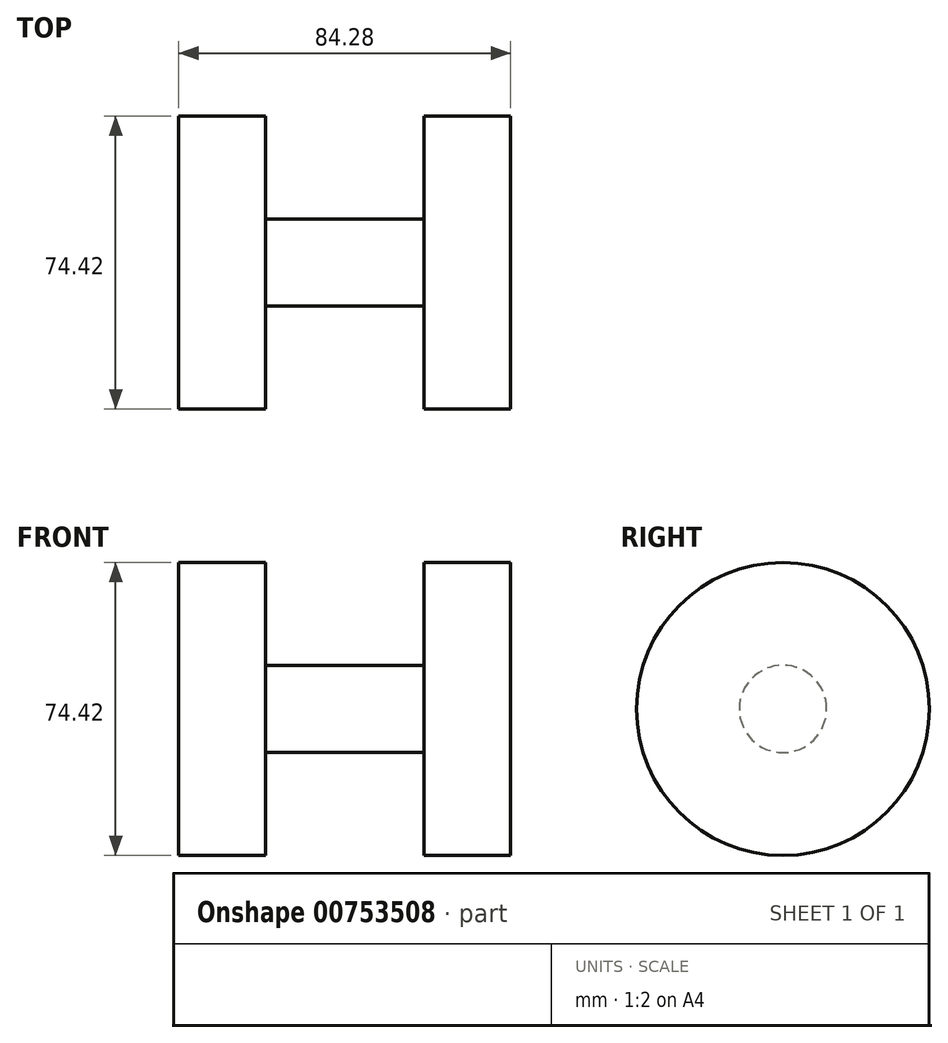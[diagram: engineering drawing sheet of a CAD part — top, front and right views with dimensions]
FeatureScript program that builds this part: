
annotation { "Feature Type Name" : "Feature", "Feature Type Description" : "" }
export const myFeature = defineFeature(function(context is Context, id is Id, definition is map)
    precondition{}
    {
        {
            var Q0;
            Q0=qCreatedBy(makeId("Front.planeOp"),FACE);
            var sketch = newSketch(context, id + "F0", { "sketchPlane" : qUnion([Q0])});
            skLineSegment(sketch, "E0.bottom", {"start": v(0, 0) * mm, "end": v(-20.13, 0) * mm});
            skLineSegment(sketch, "E0.top", {"start": v(0, 11.09) * mm, "end": v(-20.13, 11.09) * mm});
            skLineSegment(sketch, "E0.left", {"start": v(0, 0) * mm, "end": v(0, 11.09) * mm});
            skLineSegment(sketch, "E0.right", {"start": v(-20.13, 0) * mm, "end": v(-20.13, 11.09) * mm});
            skLineSegment(sketch, "E1.MirrorCS", {"start": v(0, 0) * mm, "end": v(20.13, 0) * mm});
            skLineSegment(sketch, "E2.MirrorCS", {"start": v(0, 11.09) * mm, "end": v(20.13, 11.09) * mm});
            skLineSegment(sketch, "E3.MirrorCS", {"start": v(20.13, 0) * mm, "end": v(20.13, 11.09) * mm});
            skSolve(sketch);
        }
        {
            var Q0;
            Q0 = qSketchRegion(id + "F0", true);
            var Q1;
            Q1=sQuery(id+"F0.wireOp",EDGE,"E0.bottom");
            revolve(context, id + "F1", {"surfaceOperationType" : NewSurfaceOperationType.NEW, "entities" : qUnion([Q0]), "axis" : qUnion([Q1]), "revolveType" : RevolveType.FULL});
        }
        {
            var Q0;
            Q0=qCreatedBy(makeId("Front.planeOp"),FACE);
            var sketch = newSketch(context, id + "F2", { "sketchPlane" : qUnion([Q0])});
            skLineSegment(sketch, "E4.bottom", {"start": v(-20.13, 0) * mm, "end": v(-42.14, 0) * mm});
            skLineSegment(sketch, "E4.top", {"start": v(-20.13, 37.21) * mm, "end": v(-42.14, 37.21) * mm});
            skLineSegment(sketch, "E4.left", {"start": v(-20.13, 0) * mm, "end": v(-20.13, 37.21) * mm});
            skLineSegment(sketch, "E4.right", {"start": v(-42.14, 0) * mm, "end": v(-42.14, 37.21) * mm});
            skLineSegment(sketch, "E5.MirrorCS", {"start": v(20.13, 0) * mm, "end": v(42.14, 0) * mm});
            skLineSegment(sketch, "E6.MirrorCS", {"start": v(20.13, 37.21) * mm, "end": v(42.14, 37.21) * mm});
            skLineSegment(sketch, "E7.MirrorCS", {"start": v(20.13, 0) * mm, "end": v(20.13, 37.21) * mm});
            skLineSegment(sketch, "E8.MirrorCS", {"start": v(42.14, 0) * mm, "end": v(42.14, 37.21) * mm});
            skSolve(sketch);
        }
        {
            var Q0;
            Q0 = qSketchRegion(id + "F2", true);
            var Q1;
            Q1=sQuery(id+"F2.wireOp",EDGE,"E4.bottom");
            revolve(context, id + "F3", {"operationType" : NewBodyOperationType.ADD, "surfaceOperationType" : NewSurfaceOperationType.NEW, "entities" : qUnion([Q0]), "axis" : qUnion([Q1]), "revolveType" : RevolveType.FULL});
        }
    });
